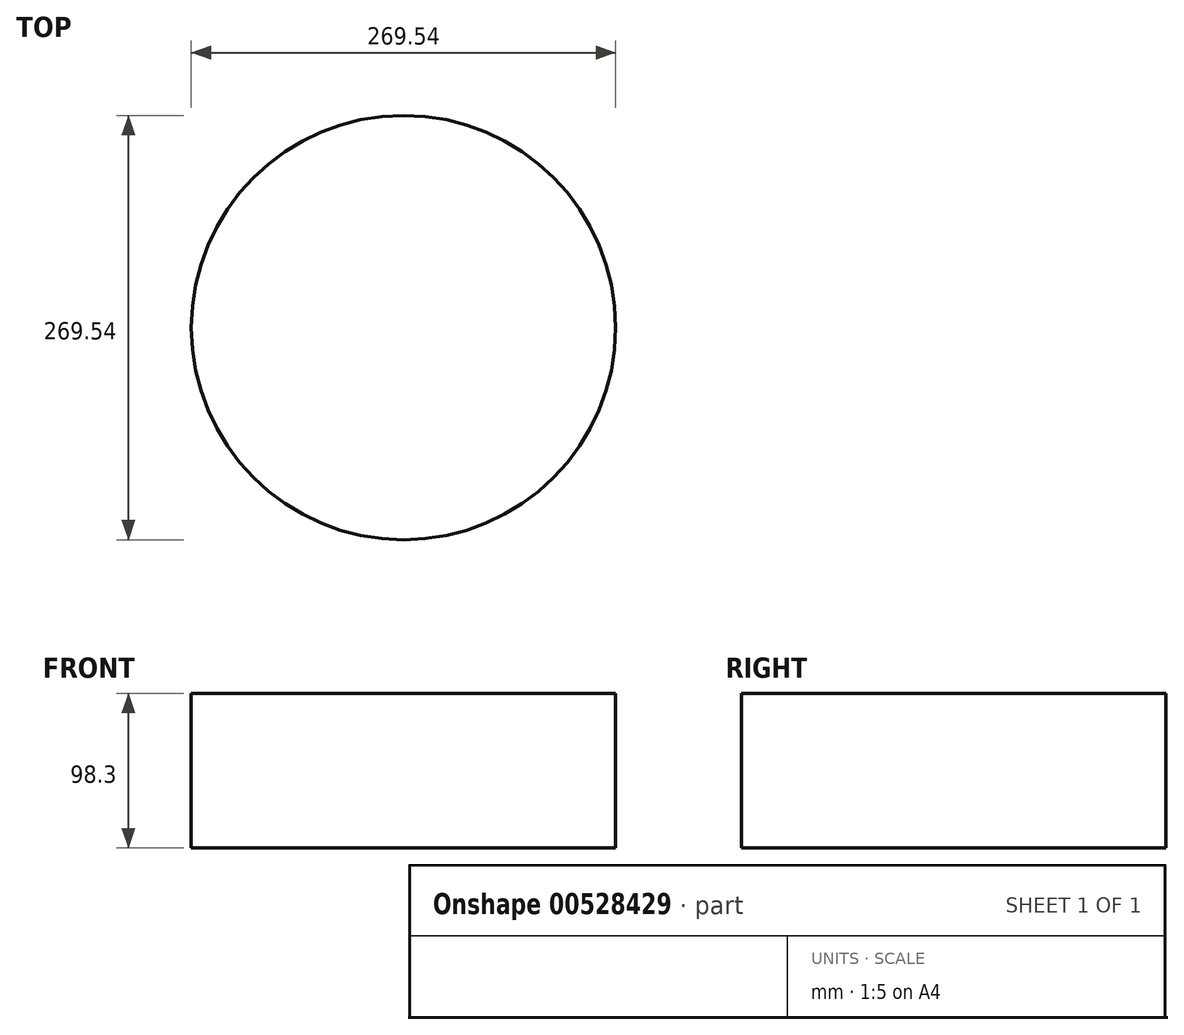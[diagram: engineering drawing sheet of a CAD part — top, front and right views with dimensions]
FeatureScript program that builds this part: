
annotation { "Feature Type Name" : "Feature", "Feature Type Description" : "" }
export const myFeature = defineFeature(function(context is Context, id is Id, definition is map)
    precondition{}
    {
        {
            var Q0;
            Q0=qCreatedBy(makeId("Top.planeOp"),FACE);
            var sketch = newSketch(context, id + "F0", { "sketchPlane" : qUnion([Q0])});
            skCircle(sketch, "E0", {"center": v(-43.85, 36.29) * mm, "radius": 134.77 * mm});
            skSolve(sketch);
        }
        {
            var Q0;
            Q0=makeQuery(id+"F0.imprint","IMPRINT",FACE,{"disambiguationData":[TD([[makeQuery(id+"F0.imprint","IMPRINT",EDGE,{"derivedFrom":sQuery(id+"F0.wireOp",EDGE,"E0")}),1.0]])]});
            extrude(context, id + "F1", {"entities" : qUnion([Q0]), "depth" : 98.3 * mm, "offsetDistance" : 25.4 * mm});
        }
    });
